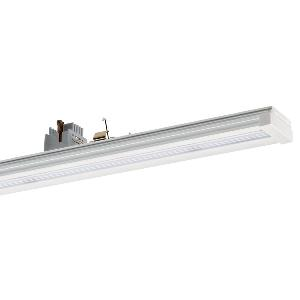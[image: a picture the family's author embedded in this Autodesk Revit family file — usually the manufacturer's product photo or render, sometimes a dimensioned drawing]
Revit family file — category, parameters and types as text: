
# Revit family: conveo_-_cvg_8000_850_w-p_ea_5_226848109-00804946_22ed
name_source: partatom
category: Lighting Fixtures
units: mm (PartAtom-declared; Revit-internal decimal feet)

## family parameters
Cut with Voids When Loaded = No
Host = Face
Light Source = No
Part Type = Normal
Room Calculation Point = No
Round Connector Dimension = Use Diameter
Shared = No

## types (1)
- CONVEO - CVG 8000/850/W-P/EA/5 (1 x LED, 8300 lm, 5000K)
    Apparent Load = 55 VA
    Approval mark = CE
    CIE Flux Codes = 54 85 97 100 100
    Color Rendering = 80-89
    Color Temperature = 5000K
    Control Gear = Electronic ballast
    Default Elevation = 1800 mm
    Description = CVG 8000/850/W-P/EA/5|Continuous-row system|light source: LED|work equipment: Electronic ballast|connected load: 220-240 V, 50-60 Hz|Power consumption: approx. 55 W|luminous flux: 8300 lm|luminous efficacy: 150 lm/W|colour temperature: Cold white, ca. 5000 K|color rendering index (CRI): >= 80|chromaticity tolerance:  3 SDCM|System of protection: IP 54|class of protection: I|technology: Switchable|luminaire body|material: Aluminium|surface: Powder coatet|colour: White|lamp cover: Acrylic (PMMA), Satine|weight (net): approx. 1.9 kg|Fastening: Available separately|minimum ambient temperature: -25 ░C|maximum ambient temperature: 47 ░C|glare control: Prism optics (linear)|Approval mark: VDE - ENEC|
    Frequency = 50 Hz
    Height = 70 mm
    Lamp = 1 x LED
    Lamp Light Flux = 8300 lm
    Lamp count = 1
    Length = 1500 mm
    Luminous efficacy = 151 lm/W
    Manufacturer = Waldmann
    ModVariant = No
    Model = 226848109-00804946
    Mounting Place = Ceiling
    Mounting Type = Pendant
    Number of Poles = 1
    OnlyDefault = Yes
    Power Factor = 1
    Product Name = CONVEO - CVG 8000/850/W-P/EA/5
    Product group = Continuous-row system (industry)
    ProductGroupID = 301
    Protection Class = Protection class I
    Protection Degree = IP 54
    RLX_Detail_Level = 1
    RlxData = <blob elided: 98977 chars, md5=79fe97e1>
    Socket = socket
    Standby Power = 0 W
    System Light Flux = 8300 lm
    System Power = 55 W
    Type Comments = Product without accessories
    Type Image = 226848079-00804943-1p5.jpg
    URL = http://relux.com
    VarID = ---
    Voltage = 230 V
    Voltage Range = 220-240 V
    Weight = 0.00 kg
    Width = 64 mm

## geometry (parser evidence)
native form markers: Blend x4, Sweep x10
no freeform markers — native parametric forms only
